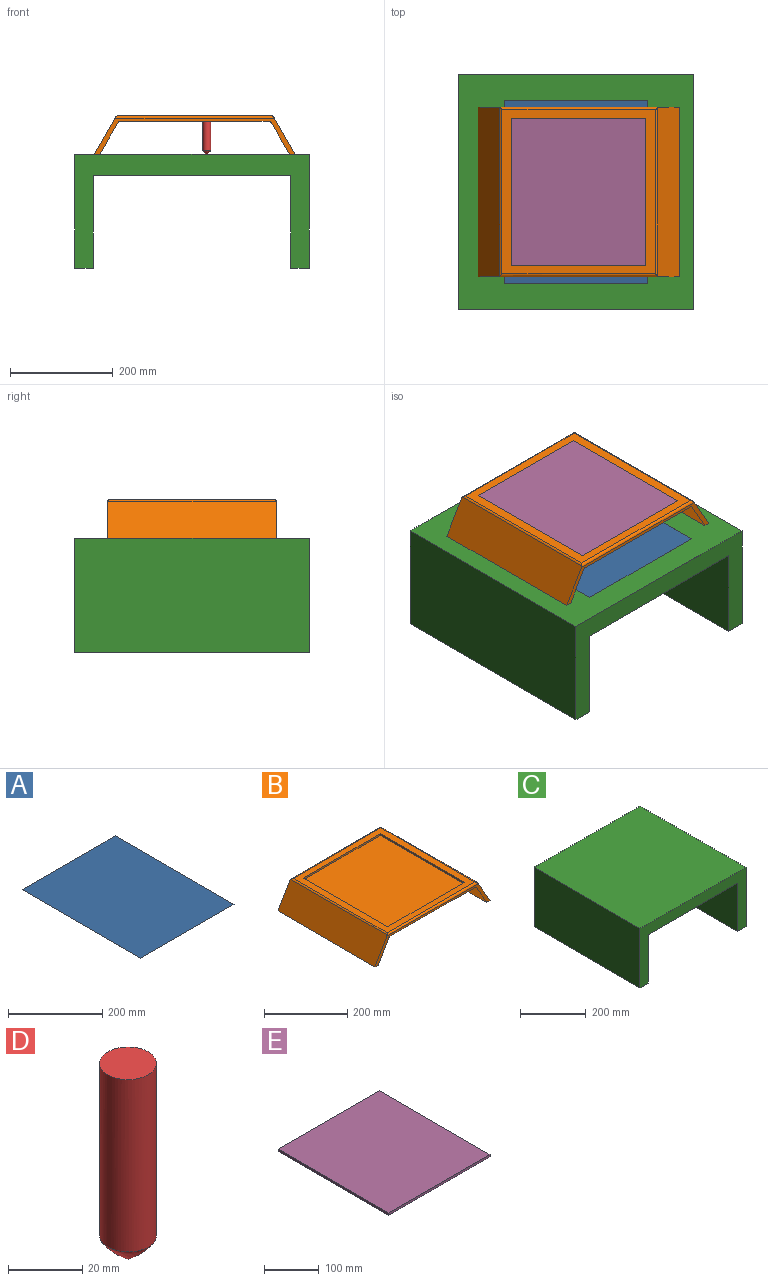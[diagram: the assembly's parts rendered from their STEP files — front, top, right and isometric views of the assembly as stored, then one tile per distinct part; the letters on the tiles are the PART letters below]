
ASSEMBLY  parts=5 mates=4
PART A: 6 faces, bbox 279.4x355.6x0 mm
  f0: plane 279.4x0.03mm, normal (0,1,0), area 7.1mm2, adj f1,f3,f4,f5
  f1: plane 355.6x0.03mm, normal (-1,0,0), area 9mm2, adj f0,f2,f4,f5
  f2: plane 279.4x0.03mm, normal (0,-1,0), area 7.1mm2, adj f1,f3,f4,f5
  f3: plane 355.6x0.03mm, normal (1,0,0), area 9mm2, adj f0,f2,f4,f5
  f4: plane 355.6x279.4mm, normal (0,0,1), area 99354.6mm2, adj f0,f1,f2,f3
  f5: plane 355.6x279.4mm, normal (0,0,-1), area 99354.6mm2, adj f0,f1,f2,f3
PART B: 21 faces, bbox 391.7x330.2x75.4 mm
  f0: plane 320.04x298.93mm, normal (0,0,1), area 20449.1mm2, adj f10,f11,f12,f13,f17,f18,f19,f20
  f1: plane 330.2x289.67mm, normal (0,0,-1), area 95648mm2, adj f2,f3,f15,f16
  f2: plane 391.71x70.36mm, normal (0,1,0), area 3246.6mm2, adj f1,f4,f5,f6,f7,f8,f9,f15
  f3: plane 391.71x70.36mm, normal (0,-1,0), area 3246.6mm2, adj f1,f4,f5,f6,f7,f8,f9,f15
  f4: plane 330.2x61.97mm, normal (-0.87,0,-0.5), area 23615.5mm2, adj f2,f3,f6,f15
  f5: plane 330.2x72.89mm, normal (0.87,0,0.5), area 27776.2mm2, adj f2,f3,f6,f17,f19,f20
  f6: plane 330.2x10.92mm, normal (0,0,-1), area 3606.4mm2, adj f2,f3,f4,f5
  f7: plane 330.2x61.97mm, normal (0.87,0,-0.5), area 23615.5mm2, adj f2,f3,f8,f16
  f8: plane 330.2x10.92mm, normal (0,0,-1), area 3606.4mm2, adj f2,f3,f7,f9
  f9: plane 330.2x72.89mm, normal (-0.87,0,0.5), area 27776.2mm2, adj f2,f3,f8,f17,f18,f20
  f10: plane 261.86x5.08mm, normal (0,-1,0), area 1330.2mm2, adj f0,f11,f13,f14
  f11: plane 287.26x5.08mm, normal (1,0,0), area 1459.3mm2, adj f0,f10,f12,f14
  f12: plane 261.86x5.08mm, normal (0,1,0), area 1330.2mm2, adj f0,f11,f13,f14
  f13: plane 287.26x5.08mm, normal (-1,0,0), area 1459.3mm2, adj f0,f10,f12,f14
  f14: plane 287.26x261.86mm, normal (0,0,1), area 75219.7mm2, adj f10,f11,f12,f13
  f15: cylinder r=5.08mm len=330.2mm, axis (0,-1,0), area 1758.2mm2, adj f1,f2,f3,f4
  f16: cylinder r=5.08mm len=330.2mm, axis (0,1,0), area 1758.2mm2, adj f1,f2,f3,f7
  f17: cylinder r=5.08mm len=310.65mm, axis (1,0,0), area 2438.3mm2, adj f0,f2,f5,f9,f18,f19
  f18: cylinder r=5.08mm len=328.84mm, axis (0,1,0), area 1730mm2, adj f0,f9,f17,f20
  f19: cylinder r=5.08mm len=328.84mm, axis (0,-1,0), area 1730mm2, adj f0,f5,f17,f20
  f20: cylinder r=5.08mm len=310.65mm, axis (-1,0,0), area 2438.3mm2, adj f0,f3,f5,f9,f18,f19
PART C: 10 faces, bbox 457.2x457.2x221.7 mm
  f0: plane 457.2x180.58mm, normal (1,0,0), area 82559.4mm2, adj f1,f7,f8,f9
  f1: plane 457.2x384.43mm, normal (0,0,-1), area 175761.6mm2, adj f0,f2,f8,f9
  f2: plane 457.2x180.58mm, normal (-1,0,0), area 82559.4mm2, adj f1,f3,f8,f9
  f3: plane 457.2x36.38mm, normal (0,0,-1), area 16635.1mm2, adj f2,f4,f8,f9
  f4: plane 457.2x221.68mm, normal (1,0,0), area 101350.9mm2, adj f3,f5,f8,f9
  f5: plane 457.2x457.2mm, normal (0,0,1), area 209031.8mm2, adj f4,f6,f8,f9
  f6: plane 457.2x221.68mm, normal (-1,0,0), area 101350.9mm2, adj f5,f7,f8,f9
  f7: plane 457.2x36.38mm, normal (0,0,-1), area 16635.1mm2, adj f0,f6,f8,f9
  f8: plane 457.2x221.68mm, normal (0,-1,0), area 31931.9mm2, adj f0,f1,f2,f3,f4,f5,f6,f7
  f9: plane 457.2x221.68mm, normal (0,1,0), area 31931.9mm2, adj f0,f1,f2,f3,f4,f5,f6,f7
PART D: 4 faces, bbox 15.3x15.3x64.6 mm
  f0: cylinder r=7.65mm len=56.9mm, axis (0,0,-1), area 2736mm2, adj f1,f3
  f1: plane 15.31x15.31mm, normal (0,0,1), area 184mm2, adj f0
  f2: plane 0.11x0.11mm, normal (0,0,-1), area 0mm2, adj f3
  f3: bspline ~15.31x15.3mm, area 280.7mm2, adj f0,f2
PART E: 6 faces, bbox 261.9x287.3x5.1 mm
  f0: plane 261.86x5.08mm, normal (0,1,0), area 1330.2mm2, adj f1,f3,f4,f5
  f1: plane 287.26x5.08mm, normal (-1,0,0), area 1459.3mm2, adj f0,f2,f4,f5
  f2: plane 261.86x5.08mm, normal (0,-1,0), area 1330.2mm2, adj f1,f3,f4,f5
  f3: plane 287.26x5.08mm, normal (1,0,0), area 1459.3mm2, adj f0,f2,f4,f5
  f4: plane 287.26x261.86mm, normal (0,0,-1), area 75219.7mm2, adj f0,f1,f2,f3
  f5: plane 287.26x261.86mm, normal (0,0,1), area 75219.7mm2, adj f0,f1,f2,f3
PLACE A rot(axis=(0,0,1),180deg) t=(273.83,101.12,221.68)mm
PLACE B t=(152.17,-101.12,221.68)mm
PLACE C t=(183.58,0,104.58)mm
PLACE D rot(axis=(0,0,-1),90deg) t=(137.99,213.28,221.68)mm
PLACE E t=(152.17,-101.12,221.68)mm
MATE fastened E.f4 <-> B.f14  axis (0,0,-1) through (215.59,0,292.04)mm
MATE fastened C.f5 <-> A.f5  axis (0,0,1) through (210.41,0,221.68)mm
MATE fastened B.f6 <-> C.f5  axis (0,0,-1) through (405.99,0,221.68)mm
MATE parallel B.f1 <-> D.f0  axis (0,0,-1) through (215.59,0,286.19)mm
